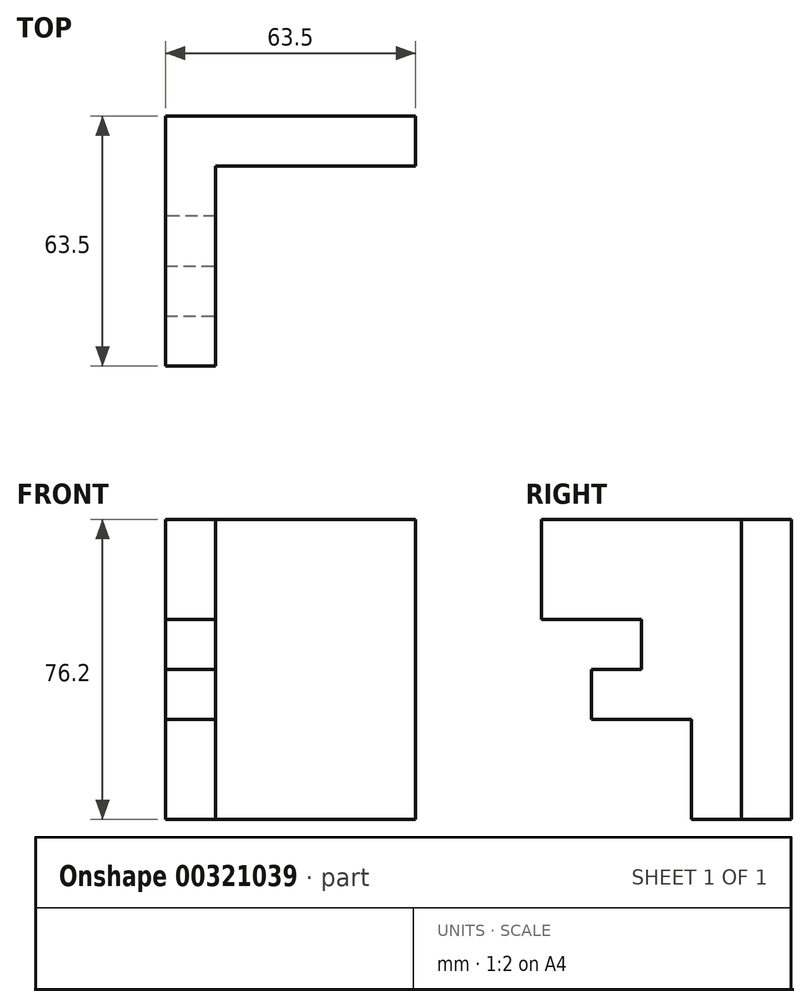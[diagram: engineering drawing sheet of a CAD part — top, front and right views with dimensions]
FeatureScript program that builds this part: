
annotation { "Feature Type Name" : "Feature", "Feature Type Description" : "" }
export const myFeature = defineFeature(function(context is Context, id is Id, definition is map)
    precondition{}
    {
        {
            var Q0;
            Q0=qCreatedBy(makeId("Right.planeOp"),FACE);
            var sketch = newSketch(context, id + "F0", { "sketchPlane" : qUnion([Q0])});
            skLineSegment(sketch, "E0", {"start": v(-39.31, -23.8) * mm, "end": v(-26.61, -23.8) * mm});
            skLineSegment(sketch, "E1", {"start": v(-26.61, -23.8) * mm, "end": v(-26.61, 52.4) * mm});
            skLineSegment(sketch, "E2", {"start": v(-26.61, 52.4) * mm, "end": v(-39.31, 52.4) * mm});
            skLineSegment(sketch, "E3", {"start": v(-39.31, 52.4) * mm, "end": v(-39.31, -23.8) * mm});
            skSolve(sketch);
        }
        {
            var Q0;
            Q0=makeQuery(id+"F0.imprint","IMPRINT",FACE,{"disambiguationData":[TD([[makeQuery(id+"F0.imprint","IMPRINT",EDGE,{"derivedFrom":sQuery(id+"F0.wireOp",EDGE,"E0")}),1.0]])]});
            extrude(context, id + "F1", {"entities" : qUnion([Q0]), "depth" : 63.5 * mm});
        }
        {
            var Q0;
            Q0=makeQuery(id+"F1.opExtrude","SWEPT_FACE",FACE,{"disambiguationData":[OSD([sQuery(id+"F0.wireOp",EDGE,"E3")])]});
            var sketch = newSketch(context, id + "F2", { "sketchPlane" : qUnion([Q0])});
            skLineSegment(sketch, "E4", {"start": v(0, 52.4) * mm, "end": v(12.7, 52.4) * mm});
            skLineSegment(sketch, "E5", {"start": v(12.7, 52.4) * mm, "end": v(12.7, -23.8) * mm});
            skLineSegment(sketch, "E6", {"start": v(12.7, -23.8) * mm, "end": v(0, -23.8) * mm});
            skLineSegment(sketch, "E7", {"start": v(0, -23.8) * mm, "end": v(0, 52.4) * mm});
            skSolve(sketch);
        }
        {
            var Q0;
            Q0=makeQuery(id+"F2.imprint","IMPRINT",FACE,{"disambiguationData":[TD([[makeQuery(id+"F2.imprint","IMPRINT",EDGE,{"derivedFrom":sQuery(id+"F2.wireOp",EDGE,"E4")}),1.0]])]});
            extrude(context, id + "F3", {"entities" : qUnion([Q0]), "operationType" : NewBodyOperationType.ADD, "depth" : 50.8 * mm});
        }
        {
            var Q0;
            Q0=makeQuery(id+"F3.opExtrude","CAP_FACE",FACE,{"disambiguationData":[OSD([sQuery(id+"F2.wireOp",EDGE,"E4"),sQuery(id+"F2.wireOp",EDGE,"E5"),sQuery(id+"F2.wireOp",EDGE,"E6"),sQuery(id+"F2.wireOp",EDGE,"E7")])],"isStart":false});
            var sketch = newSketch(context, id + "F4", { "sketchPlane" : qUnion([Q0])});
            skLineSegment(sketch, "E8", {"start": v(0, -23.8) * mm, "end": v(0, 1.6) * mm});
            skLineSegment(sketch, "E9", {"start": v(0, 1.6) * mm, "end": v(12.7, 1.6) * mm});
            skLineSegment(sketch, "E10", {"start": v(12.7, 1.6) * mm, "end": v(12.7, -23.8) * mm});
            skLineSegment(sketch, "E11", {"start": v(12.7, -23.8) * mm, "end": v(0, -23.8) * mm});
            skSolve(sketch);
        }
        {
            var Q0;
            Q0=makeQuery(id+"F4.imprint","IMPRINT",FACE,{"disambiguationData":[TD([[makeQuery(id+"F4.imprint","IMPRINT",EDGE,{"derivedFrom":sQuery(id+"F4.wireOp",EDGE,"E8")}),1.0]])]});
            extrude(context, id + "F5", {"entities" : qUnion([Q0]), "operationType" : NewBodyOperationType.REMOVE, "oppositeDirection" : true, "depth" : 38.1 * mm});
        }
        {
            var Q0;
            Q0=makeQuery(id+"F3.opExtrude","CAP_FACE",FACE,{"disambiguationData":[OSD([sQuery(id+"F2.wireOp",EDGE,"E4"),sQuery(id+"F2.wireOp",EDGE,"E5"),sQuery(id+"F2.wireOp",EDGE,"E6"),sQuery(id+"F2.wireOp",EDGE,"E7")])],"isStart":false});
            var sketch = newSketch(context, id + "F6", { "sketchPlane" : qUnion([Q0])});
            skLineSegment(sketch, "E12", {"start": v(12.7, 1.6) * mm, "end": v(12.7, 14.3) * mm});
            skLineSegment(sketch, "E13", {"start": v(12.7, 14.3) * mm, "end": v(0, 14.3) * mm});
            skLineSegment(sketch, "E14", {"start": v(0, 14.3) * mm, "end": v(0, 1.6) * mm});
            skLineSegment(sketch, "E15", {"start": v(0, 1.6) * mm, "end": v(12.7, 1.6) * mm});
            skSolve(sketch);
        }
        {
            var Q0;
            Q0=makeQuery(id+"F6.imprint","IMPRINT",FACE,{"disambiguationData":[TD([[makeQuery(id+"F6.imprint","IMPRINT",EDGE,{"derivedFrom":sQuery(id+"F6.wireOp",EDGE,"E12")}),-1.0]])]});
            extrude(context, id + "F7", {"entities" : qUnion([Q0]), "operationType" : NewBodyOperationType.REMOVE, "oppositeDirection" : true, "depth" : 12.7 * mm});
        }
        {
            var Q0;
            Q0=makeQuery(id+"F3.opExtrude","CAP_FACE",FACE,{"disambiguationData":[OSD([sQuery(id+"F2.wireOp",EDGE,"E4"),sQuery(id+"F2.wireOp",EDGE,"E5"),sQuery(id+"F2.wireOp",EDGE,"E6"),sQuery(id+"F2.wireOp",EDGE,"E7")])],"isStart":false});
            var sketch = newSketch(context, id + "F8", { "sketchPlane" : qUnion([Q0])});
            skLineSegment(sketch, "E16", {"start": v(0, 14.3) * mm, "end": v(0, 27) * mm});
            skLineSegment(sketch, "E17", {"start": v(0, 27) * mm, "end": v(12.7, 27) * mm});
            skLineSegment(sketch, "E18", {"start": v(12.7, 27) * mm, "end": v(12.7, 14.3) * mm});
            skLineSegment(sketch, "E19", {"start": v(12.7, 14.3) * mm, "end": v(0, 14.3) * mm});
            skSolve(sketch);
        }
        {
            var Q0;
            Q0=makeQuery(id+"F8.imprint","IMPRINT",FACE,{"disambiguationData":[TD([[makeQuery(id+"F8.imprint","IMPRINT",EDGE,{"derivedFrom":sQuery(id+"F8.wireOp",EDGE,"E16")}),1.0]])]});
            extrude(context, id + "F9", {"entities" : qUnion([Q0]), "operationType" : NewBodyOperationType.REMOVE, "oppositeDirection" : true, "depth" : 25.4 * mm});
        }
    });
